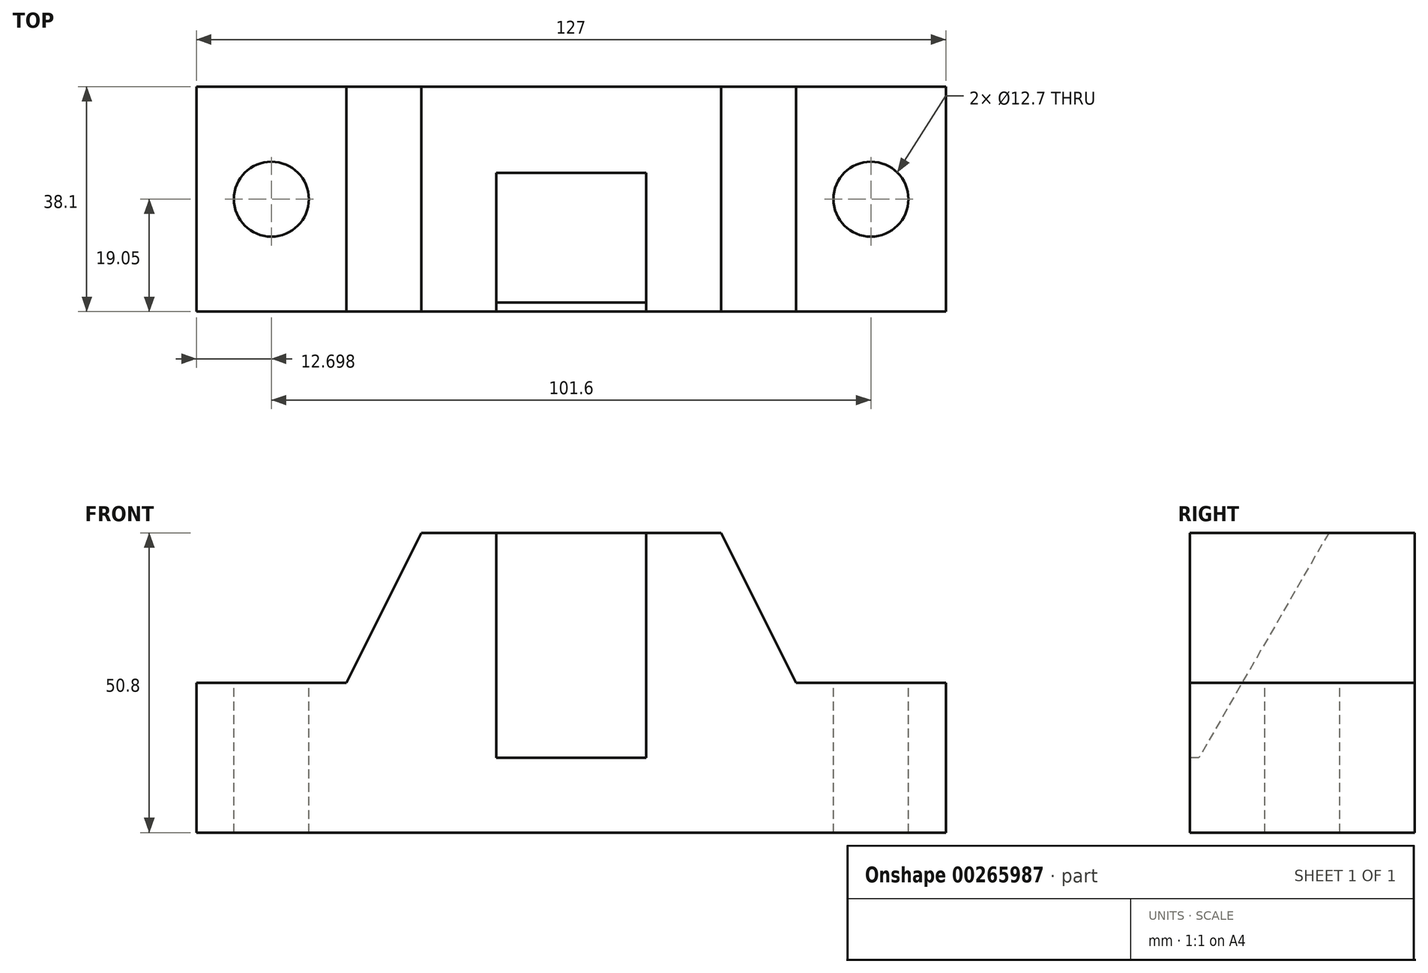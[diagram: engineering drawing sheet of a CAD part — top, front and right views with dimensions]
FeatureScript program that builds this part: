
annotation { "Feature Type Name" : "Feature", "Feature Type Description" : "" }
export const myFeature = defineFeature(function(context is Context, id is Id, definition is map)
    precondition{}
    {
        {
            var Q0;
            Q0=qCreatedBy(makeId("Front.planeOp"),FACE);
            var sketch = newSketch(context, id + "F0", { "sketchPlane" : qUnion([Q0])});
            skLineSegment(sketch, "E0", {"start": v(-65.6, -23.53) * mm, "end": v(61.4, -23.53) * mm});
            skLineSegment(sketch, "E1", {"start": v(-65.6, -23.53) * mm, "end": v(-65.6, 27.27) * mm});
            skLineSegment(sketch, "E2", {"start": v(-65.6, 27.27) * mm, "end": v(61.4, 27.27) * mm});
            skLineSegment(sketch, "E3", {"start": v(61.4, 27.27) * mm, "end": v(61.4, -23.53) * mm});
            skSolve(sketch);
        }
        {
            var Q0;
            Q0 = qSketchRegion(id + "F0", true);
            extrude(context, id + "F1", {"entities" : qUnion([Q0]), "depth" : 38.1 * mm});
        }
        {
            var Q0;
            Q0=makeQuery(id+"F1.opExtrude","CAP_FACE",FACE,{"disambiguationData":[OSD([sQuery(id+"F0.wireOp",EDGE,"E0"),sQuery(id+"F0.wireOp",EDGE,"E1"),sQuery(id+"F0.wireOp",EDGE,"E2"),sQuery(id+"F0.wireOp",EDGE,"E3")])],"isStart":false});
            var sketch = newSketch(context, id + "F2", { "sketchPlane" : qUnion([Q0])});
            skLineSegment(sketch, "E4", {"start": v(61.4, 1.87) * mm, "end": v(36, 1.87) * mm});
            skLineSegment(sketch, "E5", {"start": v(61.4, 27.27) * mm, "end": v(23.3, 27.27) * mm});
            skLineSegment(sketch, "E6", {"start": v(36, 1.87) * mm, "end": v(23.3, 27.27) * mm});
            skLineSegment(sketch, "E7", {"start": v(-65.6, 1.87) * mm, "end": v(-40.2, 1.87) * mm});
            skLineSegment(sketch, "E8", {"start": v(-65.6, 27.27) * mm, "end": v(-27.5, 27.27) * mm});
            skLineSegment(sketch, "E9", {"start": v(-27.5, 27.27) * mm, "end": v(-40.2, 1.87) * mm});
            skLineSegment(sketch, "E10", {"start": v(-65.6, 27.27) * mm, "end": v(-65.6, 1.87) * mm});
            skLineSegment(sketch, "E11", {"start": v(61.4, 27.27) * mm, "end": v(61.4, 1.87) * mm});
            skSolve(sketch);
        }
        {
            var Q0;
            Q0 = qSketchRegion(id + "F2", true);
            extrude(context, id + "F3", {"entities" : qUnion([Q0]), "operationType" : NewBodyOperationType.REMOVE, "oppositeDirection" : true, "depth" : 38.1 * mm});
        }
        {
            var Q0;
            Q0=makeQuery(id+"F3.boolean.opBoolean","COPY",FACE,{"derivedFrom":makeQuery(id+"F3.opExtrude","SWEPT_FACE",FACE,{"disambiguationData":[OSD([sQuery(id+"F2.wireOp",EDGE,"E4")])]})});
            var sketch = newSketch(context, id + "F4", { "sketchPlane" : qUnion([Q0])});
            skCircle(sketch, "E12", {"center": v(48.7, -19.05) * mm, "radius": 6.35 * mm});
            skPoint(sketch, "E12.centerSnap0", {"position": v(48.7, -38.1) * mm});
            skPoint(sketch, "E12.centerSnap1", {"position": v(36, -19.05) * mm});
            skSolve(sketch);
        }
        {
            var Q0;
            Q0 = qSketchRegion(id + "F4", true);
            extrude(context, id + "F5", {"entities" : qUnion([Q0]), "operationType" : NewBodyOperationType.REMOVE, "oppositeDirection" : true, "depth" : 25.4 * mm});
        }
        {
            var Q0;
            Q0=makeQuery(id+"F3.boolean.opBoolean","COPY",FACE,{"derivedFrom":makeQuery(id+"F3.opExtrude","SWEPT_FACE",FACE,{"disambiguationData":[OSD([sQuery(id+"F2.wireOp",EDGE,"E7")])]})});
            var sketch = newSketch(context, id + "F6", { "sketchPlane" : qUnion([Q0])});
            skCircle(sketch, "E13", {"center": v(-52.9, -19.05) * mm, "radius": 6.35 * mm});
            skPoint(sketch, "E13.centerSnap0", {"position": v(-52.9, -38.1) * mm});
            skPoint(sketch, "E13.centerSnap1", {"position": v(-65.6, -19.05) * mm});
            skSolve(sketch);
        }
        {
            var Q0;
            Q0 = qSketchRegion(id + "F6", true);
            extrude(context, id + "F7", {"entities" : qUnion([Q0]), "operationType" : NewBodyOperationType.REMOVE, "oppositeDirection" : true, "depth" : 25.4 * mm});
        }
        {
            var Q0;
            Q0=makeQuery(id+"F1.opExtrude","SWEPT_FACE",FACE,{"disambiguationData":[OSD([sQuery(id+"F0.wireOp",EDGE,"E2")])]});
            var sketch = newSketch(context, id + "F8", { "sketchPlane" : qUnion([Q0])});
            skLineSegment(sketch, "E14", {"start": v(-27.5, -38.1) * mm, "end": v(-14.8, -38.1) * mm});
            skLineSegment(sketch, "E15", {"start": v(-14.8, -38.1) * mm, "end": v(10.6, -38.1) * mm});
            skLineSegment(sketch, "E16", {"start": v(-14.8, -38.1) * mm, "end": v(-14.8, 0.1) * mm});
            skLineSegment(sketch, "E17", {"start": v(-14.8, 0.1) * mm, "end": v(10.6, 0.1) * mm});
            skLineSegment(sketch, "E18", {"start": v(10.6, 0.1) * mm, "end": v(10.6, -38.1) * mm});
            skSolve(sketch);
        }
        {
            var Q0;
            Q0 = qSketchRegion(id + "F8", true);
            extrude(context, id + "F9", {"entities" : qUnion([Q0]), "operationType" : NewBodyOperationType.REMOVE, "oppositeDirection" : true, "depth" : 38.1 * mm});
        }
        {
            var Q0;
            Q0=makeQuery(id+"F9.boolean.opBoolean","COPY",FACE,{"derivedFrom":makeQuery(id+"F9.opExtrude","SWEPT_FACE",FACE,{"disambiguationData":[OSD([sQuery(id+"F8.wireOp",EDGE,"E16")])]})});
            var sketch = newSketch(context, id + "F10", { "sketchPlane" : qUnion([Q0])});
            skLineSegment(sketch, "E19", {"start": v(-38.1, -10.83) * mm, "end": v(-38.1, 27.27) * mm});
            skLineSegment(sketch, "E20", {"start": v(-38.1, 27.27) * mm, "end": v(-14.57, 27.27) * mm});
            skLineSegment(sketch, "E21", {"start": v(-14.57, 27.27) * mm, "end": v(-38.1, -13.48) * mm});
            skLineSegment(sketch, "E22", {"start": v(-14.57, 27.27) * mm, "end": v(0, 27.27) * mm});
            skLineSegment(sketch, "E23", {"start": v(0, 27.27) * mm, "end": v(0, -10.83) * mm});
            skLineSegment(sketch, "E24", {"start": v(0, -10.83) * mm, "end": v(-38.1, -10.83) * mm});
            skSolve(sketch);
        }
        {
            var Q0;
            {var subQ0=sQuery(id+"F10.wireOp",EDGE,"E22");Q0=makeQuery(id+"F10.imprint","IMPRINT",FACE,{"disambiguationData":[TD([[makeQuery(id+"F10.imprint","IMPRINT",EDGE,{"derivedFrom":subQ0}),-1.0]])]});}
            extrude(context, id + "F11", {"entities" : qUnion([Q0]), "operationType" : NewBodyOperationType.ADD, "depth" : 25.4 * mm});
        }
    });
